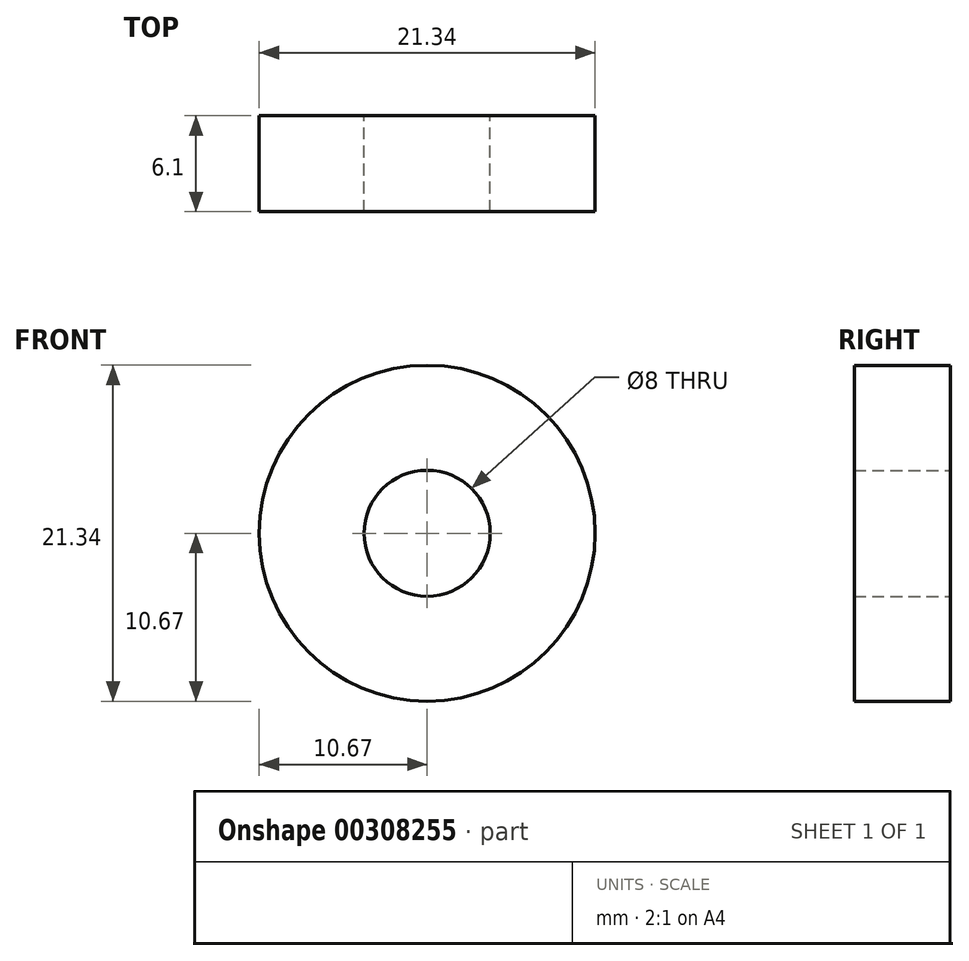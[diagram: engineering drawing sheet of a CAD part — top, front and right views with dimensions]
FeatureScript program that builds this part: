
annotation { "Feature Type Name" : "Feature", "Feature Type Description" : "" }
export const myFeature = defineFeature(function(context is Context, id is Id, definition is map)
    precondition{}
    {
        {
            var Q0;
            Q0=qCreatedBy(makeId("Front.planeOp"),FACE);
            var sketch = newSketch(context, id + "F0", { "sketchPlane" : qUnion([Q0])});
            skCircle(sketch, "E0", {"center": v(0, 0) * mm, "radius": 10.67 * mm});
            skCircle(sketch, "E1", {"center": v(0, 0) * mm, "radius": 4 * mm});
            skSolve(sketch);
        }
        {
            var Q0;
            Q0 = qSketchRegion(id + "F0", true);
            extrude(context, id + "F1", {"entities" : qUnion([Q0]), "depth" : 6.1 * mm});
        }
    });
